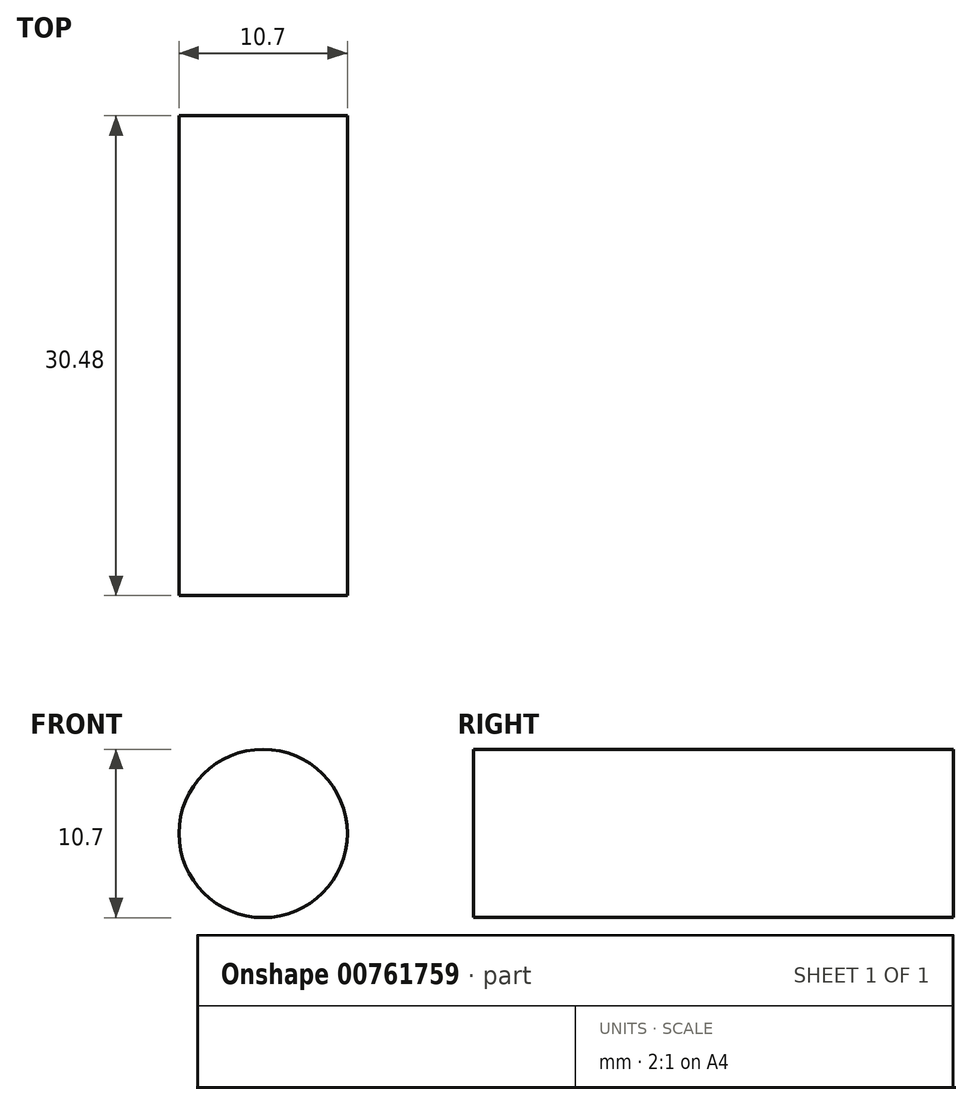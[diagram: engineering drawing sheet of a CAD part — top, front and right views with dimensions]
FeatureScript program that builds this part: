
annotation { "Feature Type Name" : "Feature", "Feature Type Description" : "" }
export const myFeature = defineFeature(function(context is Context, id is Id, definition is map)
    precondition{}
    {
        {
            var Q0;
            Q0=qCreatedBy(makeId("Front.planeOp"),FACE);
            var sketch = newSketch(context, id + "F0", { "sketchPlane" : qUnion([Q0])});
            skCircle(sketch, "E0", {"center": v(0, 0) * mm, "radius": 5.35 * mm});
            skSolve(sketch);
        }
        {
            var Q0;
            Q0=makeQuery(id+"F0.imprint","IMPRINT",FACE,{"disambiguationData":[TD([[makeQuery(id+"F0.imprint","IMPRINT",EDGE,{"derivedFrom":sQuery(id+"F0.wireOp",EDGE,"E0")}),1.0]])]});
            extrude(context, id + "F1", {"entities" : qUnion([Q0]), "depth" : 30.48 * mm, "offsetDistance" : 25.4 * mm});
        }
    });
